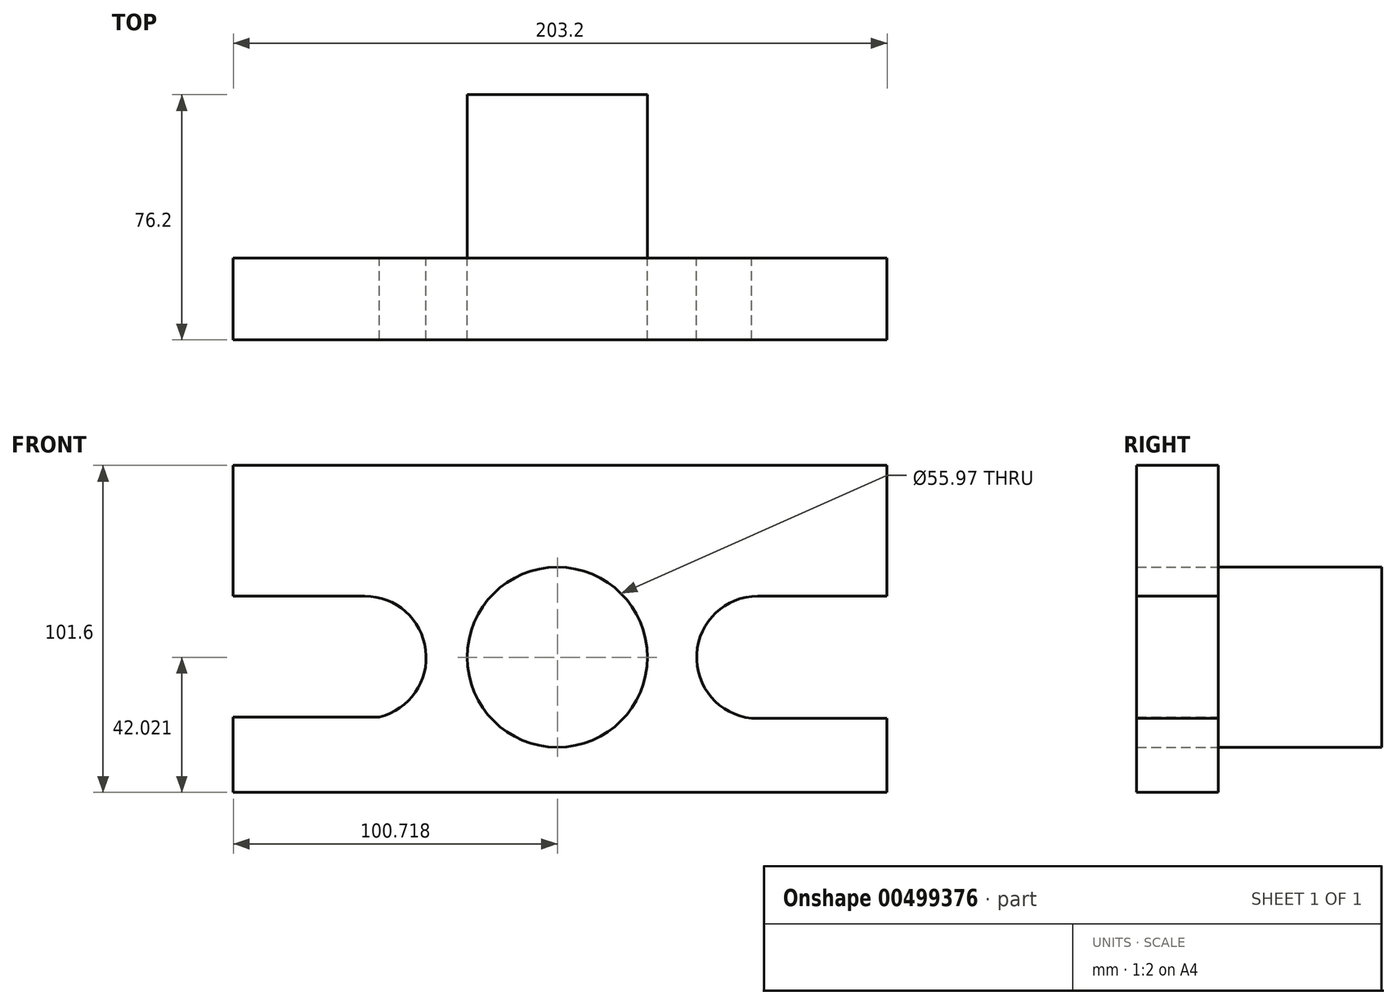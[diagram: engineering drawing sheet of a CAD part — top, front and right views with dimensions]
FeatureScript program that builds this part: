
annotation { "Feature Type Name" : "Feature", "Feature Type Description" : "" }
export const myFeature = defineFeature(function(context is Context, id is Id, definition is map)
    precondition{}
    {
        {
            var Q0;
            Q0=qCreatedBy(makeId("Front.planeOp"),FACE);
            var sketch = newSketch(context, id + "F0", { "sketchPlane" : qUnion([Q0])});
            skLineSegment(sketch, "E0.bottom", {"start": v(-137.36, 84.07) * mm, "end": v(65.84, 84.07) * mm});
            skLineSegment(sketch, "E0.top", {"start": v(-137.36, -17.53) * mm, "end": v(65.84, -17.53) * mm});
            skLineSegment(sketch, "E0.left", {"start": v(-137.36, 84.07) * mm, "end": v(-137.36, -17.53) * mm});
            skLineSegment(sketch, "E0.right", {"start": v(65.84, 84.07) * mm, "end": v(65.84, -17.53) * mm});
            skLineSegment(sketch, "E1", {"start": v(-137.36, 43.48) * mm, "end": v(-96.47, 43.48) * mm});
            skLineSegment(sketch, "E2", {"start": v(25.7, 43.48) * mm, "end": v(65.84, 43.48) * mm});
            skPoint(sketch, "E3.visualSharp", {"position": v(-64.04, 43.48) * mm});
            skArc(sketch, "E3.filletArc", {"start": v(-91.95, 5.92) * mm, "mid": v(-77.56, 26.7) * mm, "end": v(-96.47, 43.48) * mm});
            skPoint(sketch, "E4.visualSharp", {"position": v(0, 43.48) * mm});
            skArc(sketch, "E4.filletArc", {"start": v(25.7, 43.48) * mm, "mid": v(6.68, 25.42) * mm, "end": v(23.72, 5.48) * mm});
            skLineSegment(sketch, "E5", {"start": v(-91.95, 5.92) * mm, "end": v(-137.36, 5.92) * mm});
            skLineSegment(sketch, "E6", {"start": v(23.72, 5.48) * mm, "end": v(65.84, 5.48) * mm});
            skCircle(sketch, "E7", {"center": v(-36.64, 24.5) * mm, "radius": 27.99 * mm});
            skSolve(sketch);
        }
        {
            var Q0;
            {var subQ5=sQuery(id+"F0.wireOp",EDGE,"E0.bottom");Q0=makeQuery(id+"F0.imprint","IMPRINT",FACE,{"disambiguationData":[TD([[makeQuery(id+"F0.imprint","IMPRINT",EDGE,{"derivedFrom":subQ5}),-1.0]])]});}
            extrude(context, id + "F1", {"entities" : qUnion([Q0]), "depth" : 25.4 * mm});
        }
        {
            var Q0;
            Q0=makeQuery(id+"F0.imprint","IMPRINT",FACE,{"disambiguationData":[TD([[makeQuery(id+"F0.imprint","IMPRINT",EDGE,{"derivedFrom":sQuery(id+"F0.wireOp",EDGE,"E7")}),1.0]])]});
            extrude(context, id + "F2", {"entities" : qUnion([Q0]), "operationType" : NewBodyOperationType.ADD, "oppositeDirection" : true, "depth" : 25.4 * mm});
        }
        {
            var Q0;
            Q0=makeQuery(id+"F2.opExtrude","CAP_FACE",FACE,{"disambiguationData":[OSD([sQuery(id+"F0.wireOp",EDGE,"E7")])],"isStart":false});
            extrude(context, id + "F3", {"entities" : qUnion([Q0]), "operationType" : NewBodyOperationType.ADD, "depth" : 25.4 * mm});
        }
    });
